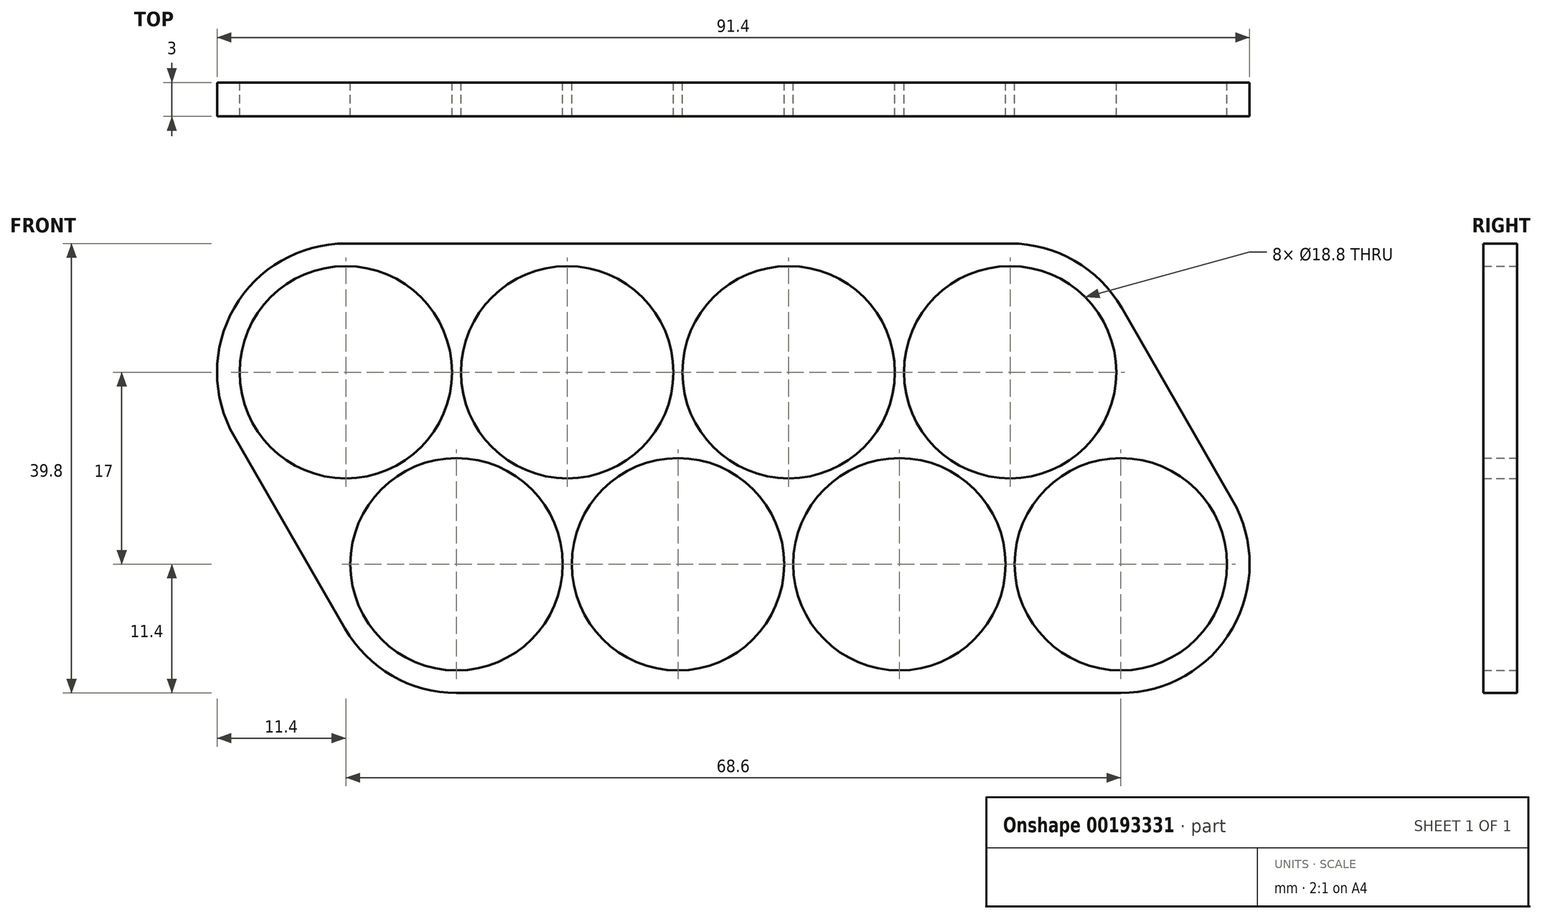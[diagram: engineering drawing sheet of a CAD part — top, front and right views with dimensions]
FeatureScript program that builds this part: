
annotation { "Feature Type Name" : "Feature", "Feature Type Description" : "" }
export const myFeature = defineFeature(function(context is Context, id is Id, definition is map)
    precondition{}
    {
        {
            var Q0;
            Q0=qCreatedBy(makeId("Front.planeOp"),FACE);
            var sketch = newSketch(context, id + "F0", { "sketchPlane" : qUnion([Q0])});
            skCircle(sketch, "E0", {"center": v(0, 0) * mm, "radius": 9.4 * mm});
            skCircle(sketch, "E1.1.0.0", {"center": v(19.6, 0) * mm, "radius": 9.4 * mm});
            skCircle(sketch, "E1.2.0.0", {"center": v(39.2, 0) * mm, "radius": 9.4 * mm});
            skCircle(sketch, "E1.3.0.0", {"center": v(58.8, 0) * mm, "radius": 9.4 * mm});
            skLineSegment(sketch, "E1.direction1", {"start": v(0, 0) * mm, "end": v(19.6, 0) * mm, "construction": true});
            skLineSegment(sketch, "E2", {"start": v(0, -17) * mm, "end": v(73.2, -17) * mm, "construction": true});
            skLineSegment(sketch, "E3", {"start": v(9.8, 0) * mm, "end": v(9.8, -17) * mm, "construction": true});
            skCircle(sketch, "E4", {"center": v(9.8, -17) * mm, "radius": 9.4 * mm});
            skCircle(sketch, "E5.1.0.0", {"center": v(29.4, -17) * mm, "radius": 9.4 * mm});
            skCircle(sketch, "E5.2.0.0", {"center": v(49, -17) * mm, "radius": 9.4 * mm});
            skCircle(sketch, "E5.3.0.0", {"center": v(68.6, -17) * mm, "radius": 9.4 * mm});
            skLineSegment(sketch, "E5.direction1", {"start": v(9.8, -17) * mm, "end": v(29.4, -17) * mm, "construction": true});
            skLineSegment(sketch, "E6", {"start": v(-8.14, -4.7) * mm, "end": v(1.66, -21.7) * mm});
            skLineSegment(sketch, "E7", {"start": v(0, 9.4) * mm, "end": v(58.8, 9.4) * mm});
            skLineSegment(sketch, "E8", {"start": v(9.8, -17) * mm, "end": v(9.8, -26.4) * mm, "construction": true});
            skLineSegment(sketch, "E9", {"start": v(68.6, -17) * mm, "end": v(68.6, -26.4) * mm, "construction": true});
            skLineSegment(sketch, "E10", {"start": v(9.8, -26.4) * mm, "end": v(68.6, -26.4) * mm});
            skLineSegment(sketch, "E11", {"start": v(66.94, 4.7) * mm, "end": v(76.74, -12.3) * mm});
            skArc(sketch, "E12", {"start": v(58.8, 9.4) * mm, "mid": v(63.5, 8.14) * mm, "end": v(66.94, 4.7) * mm});
            skArc(sketch, "E13", {"start": v(76.74, -12.3) * mm, "mid": v(76.74, -21.7) * mm, "end": v(68.6, -26.4) * mm});
            skArc(sketch, "E14", {"start": v(9.8, -26.4) * mm, "mid": v(5.1, -25.14) * mm, "end": v(1.66, -21.7) * mm});
            skArc(sketch, "E15", {"start": v(-8.14, -4.7) * mm, "mid": v(-8.14, 4.7) * mm, "end": v(0, 9.4) * mm});
            skArc(sketch, "E16.0", {"start": v(0, 11.4) * mm, "mid": v(-9.87, 5.7) * mm, "end": v(-9.88, -5.7) * mm});
            skLineSegment(sketch, "E17.0", {"start": v(0, 11.4) * mm, "end": v(58.8, 11.4) * mm});
            skArc(sketch, "E18.0", {"start": v(68.68, 5.7) * mm, "mid": v(64.5, 9.87) * mm, "end": v(58.8, 11.4) * mm});
            skLineSegment(sketch, "E19.0", {"start": v(68.68, 5.7) * mm, "end": v(78.48, -11.3) * mm});
            skLineSegment(sketch, "E20.0", {"start": v(9.8, -28.4) * mm, "end": v(68.6, -28.4) * mm});
            skLineSegment(sketch, "E21.0", {"start": v(-9.88, -5.7) * mm, "end": v(-0.08, -22.7) * mm});
            skArc(sketch, "E22.0", {"start": v(-0.08, -22.7) * mm, "mid": v(4.1, -26.87) * mm, "end": v(9.8, -28.4) * mm});
            skArc(sketch, "E23.0", {"start": v(68.6, -28.4) * mm, "mid": v(78.47, -22.7) * mm, "end": v(78.48, -11.3) * mm});
            skArc(sketch, "E24.trimOffspring", {"start": v(9.8, -5.82) * mm, "mid": v(9.87, -5.71) * mm, "end": v(9.93, -5.6) * mm});
            skArc(sketch, "E25.trimOffspring", {"start": v(9.93, -5.6) * mm, "mid": v(9.86, -5.6) * mm, "end": v(9.8, -5.6) * mm});
            skLineSegment(sketch, "E26", {"start": v(39.2, 0) * mm, "end": v(49, -17) * mm, "construction": true});
            skLineSegment(sketch, "E27", {"start": v(49, -17) * mm, "end": v(55.57, -28.4) * mm, "construction": true});
            skLineSegment(sketch, "E28", {"start": v(39.2, 0) * mm, "end": v(32.63, 11.4) * mm, "construction": true});
            skSolve(sketch);
        }
        {
            var Q0;
            Q0=qSketchRegion(id+"F0",true);
            var Q1;
            {var subQ3=sQuery(id+"F0.wireOp",EDGE,"E1.1.0.0");Q1=makeQuery(id+"F0.imprint","IMPRINT",FACE,{"disambiguationData":[TD([[makeQuery(id+"F0.imprint","IMPRINT",EDGE,{"derivedFrom":subQ3}),-1.0]])]});}
            extrude(context, id + "F1", {"entities" : qUnion([Q0, Q1]), "depth" : 3 * mm});
        }
    });
